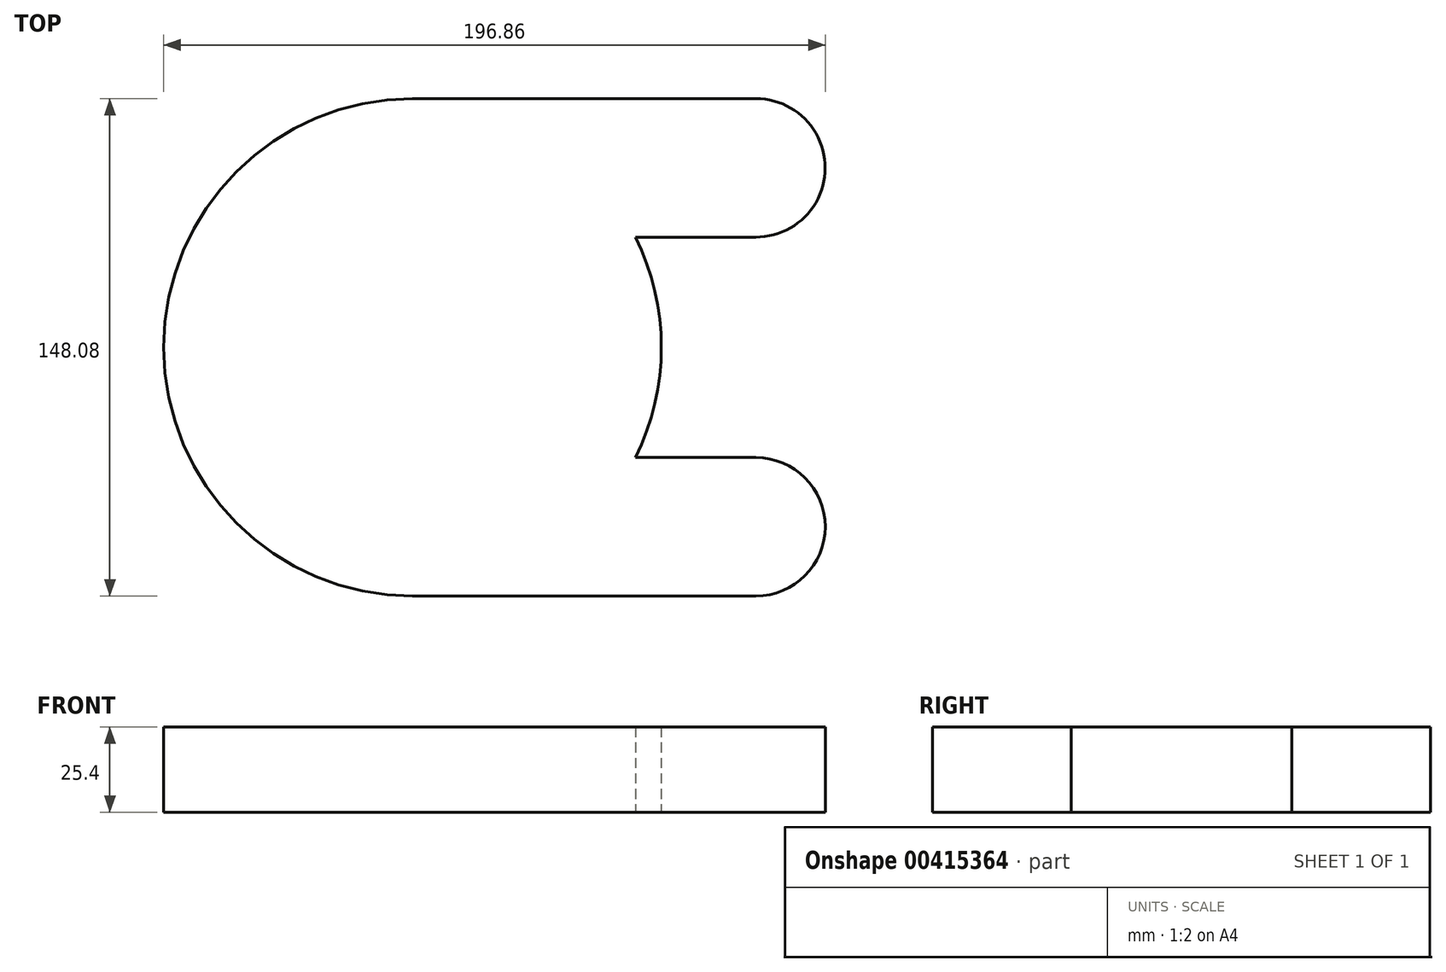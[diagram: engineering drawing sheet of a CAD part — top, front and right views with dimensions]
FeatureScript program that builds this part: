
annotation { "Feature Type Name" : "Feature", "Feature Type Description" : "" }
export const myFeature = defineFeature(function(context is Context, id is Id, definition is map)
    precondition{}
    {
        {
            var Q0;
            Q0=qCreatedBy(makeId("Top.planeOp"),FACE);
            var sketch = newSketch(context, id + "F0", { "sketchPlane" : qUnion([Q0])});
            skCircle(sketch, "E0", {"center": v(0, 0) * mm, "radius": 74.04 * mm});
            skCircle(sketch, "E1", {"center": v(0, 0) * mm, "radius": 53.43 * mm});
            skCircle(sketch, "E2", {"center": v(0, 53.43) * mm, "radius": 20.6 * mm});
            skCircle(sketch, "E3", {"center": v(0, -53.43) * mm, "radius": 20.6 * mm});
            skCircle(sketch, "E4", {"center": v(102.2, -53.43) * mm, "radius": 20.6 * mm});
            skCircle(sketch, "E5", {"center": v(102.2, 53.43) * mm, "radius": 20.6 * mm});
            skLineSegment(sketch, "E6", {"start": v(0, -53.43) * mm, "end": v(102.2, -53.43) * mm});
            skLineSegment(sketch, "E7", {"start": v(0, 53.43) * mm, "end": v(102.2, 53.43) * mm});
            skLineSegment(sketch, "E8", {"start": v(0, 0) * mm, "end": v(102.2, 0) * mm});
            skLineSegment(sketch, "E9", {"start": v(0, 74.04) * mm, "end": v(102.2, 74.04) * mm});
            skLineSegment(sketch, "E10", {"start": v(0, -74.04) * mm, "end": v(102.2, -74.04) * mm});
            skLineSegment(sketch, "E11", {"start": v(102.2, -74.04) * mm, "end": v(102.2, -74.04) * mm});
            skLineSegment(sketch, "E12", {"start": v(102.2, 74.04) * mm, "end": v(102.2, 53.43) * mm});
            skLineSegment(sketch, "E13", {"start": v(102.2, 0) * mm, "end": v(102.2, 53.43) * mm});
            skLineSegment(sketch, "E14", {"start": v(102.2, 0) * mm, "end": v(102.2, -53.43) * mm});
            skLineSegment(sketch, "E15", {"start": v(102.2, -53.43) * mm, "end": v(102.2, -74.04) * mm});
            skLineSegment(sketch, "E16", {"start": v(102.2, -32.82) * mm, "end": v(0, -32.82) * mm});
            skLineSegment(sketch, "E17", {"start": v(0.09, 32.82) * mm, "end": v(102.2, 32.82) * mm});
            skSolve(sketch);
        }
        {
            var Q0;
            {var subQ0=sQuery(id+"F0.wireOp",EDGE,"E1");var subQ1=makeQuery(id+"F0.imprint","INTERSECT",VERTEX,{"derivedFrom":[subQ0,sQuery(id+"F0.wireOp",EDGE,"E8")]});Q0=makeQuery(id+"F0.imprint","IMPRINT",FACE,{"disambiguationData":[TD([[makeQuery(id+"F0.imprint","IMPRINT",EDGE,{"disambiguationData":[TD([[subQ1,-1.0]])],"derivedFrom":subQ0}),1.0]])]});}
            var Q1;
            {var subQ0=sQuery(id+"F0.wireOp",EDGE,"E1");var subQ1=makeQuery(id+"F0.imprint","INTERSECT",VERTEX,{"derivedFrom":[subQ0,sQuery(id+"F0.wireOp",EDGE,"E6")]});Q1=makeQuery(id+"F0.imprint","IMPRINT",FACE,{"disambiguationData":[TD([[makeQuery(id+"F0.imprint","IMPRINT",EDGE,{"disambiguationData":[TD([[subQ1,1.0]])],"derivedFrom":subQ0}),1.0]])]});}
            var Q2;
            {var subQ0=sQuery(id+"F0.wireOp",EDGE,"E3");var subQ1=sQuery(id+"F0.wireOp",EDGE,"E1");var subQ2=makeQuery(id+"F0.imprint","INTERSECT",VERTEX,{"disambiguationData":[OD(1.0)],"derivedFrom":[subQ1,subQ0]});Q2=makeQuery(id+"F0.imprint","IMPRINT",FACE,{"disambiguationData":[TD([[makeQuery(id+"F0.imprint","IMPRINT",EDGE,{"disambiguationData":[TD([[subQ2,-1.0]])],"derivedFrom":subQ1}),1.0]])]});}
            var Q3;
            {var subQ0=sQuery(id+"F0.wireOp",EDGE,"E6");var subQ1=sQuery(id+"F0.wireOp",EDGE,"E1");var subQ2=makeQuery(id+"F0.imprint","INTERSECT",VERTEX,{"derivedFrom":[subQ1,subQ0]});Q3=makeQuery(id+"F0.imprint","IMPRINT",FACE,{"disambiguationData":[TD([[makeQuery(id+"F0.imprint","IMPRINT",EDGE,{"disambiguationData":[TD([[subQ2,-1.0]])],"derivedFrom":subQ1}),-1.0]])]});}
            var Q4;
            {var subQ3=sQuery(id+"F0.wireOp",EDGE,"E6");var subQ7=sQuery(id+"F0.wireOp",EDGE,"E0");var subQ8=makeQuery(id+"F0.imprint","INTERSECT",VERTEX,{"derivedFrom":[subQ7,subQ3]});Q4=makeQuery(id+"F0.imprint","IMPRINT",FACE,{"disambiguationData":[TD([[makeQuery(id+"F0.imprint","IMPRINT",EDGE,{"disambiguationData":[TD([[subQ8,-1.0]])],"derivedFrom":subQ7}),1.0]])]});}
            var Q5;
            {var subQ1=sQuery(id+"F0.wireOp",EDGE,"E4");var subQ3=sQuery(id+"F0.wireOp",EDGE,"E6");var subQ4=makeQuery(id+"F0.imprint","INTERSECT",VERTEX,{"derivedFrom":[subQ1,subQ3]});Q5=makeQuery(id+"F0.imprint","IMPRINT",FACE,{"disambiguationData":[TD([[makeQuery(id+"F0.imprint","IMPRINT",EDGE,{"disambiguationData":[TD([[subQ4,1.0]])],"derivedFrom":subQ1}),1.0]])]});}
            var Q6;
            {var subQ0=sQuery(id+"F0.wireOp",EDGE,"E7");var subQ1=sQuery(id+"F0.wireOp",EDGE,"E1");var subQ2=makeQuery(id+"F0.imprint","INTERSECT",VERTEX,{"derivedFrom":[subQ1,subQ0]});Q6=makeQuery(id+"F0.imprint","IMPRINT",FACE,{"disambiguationData":[TD([[makeQuery(id+"F0.imprint","IMPRINT",EDGE,{"disambiguationData":[TD([[subQ2,-1.0]])],"derivedFrom":subQ1}),-1.0]])]});}
            var Q7;
            {var subQ1=sQuery(id+"F0.wireOp",EDGE,"E0");var subQ3=sQuery(id+"F0.wireOp",EDGE,"E7");var subQ4=makeQuery(id+"F0.imprint","INTERSECT",VERTEX,{"derivedFrom":[subQ1,subQ3]});Q7=makeQuery(id+"F0.imprint","IMPRINT",FACE,{"disambiguationData":[TD([[makeQuery(id+"F0.imprint","IMPRINT",EDGE,{"disambiguationData":[TD([[subQ4,1.0]])],"derivedFrom":subQ3}),1.0]])]});}
            var Q8;
            {var subQ0=sQuery(id+"F0.wireOp",EDGE,"E15");Q8=makeQuery(id+"F0.imprint","IMPRINT",FACE,{"disambiguationData":[TD([[makeQuery(id+"F0.imprint","IMPRINT",EDGE,{"derivedFrom":subQ0}),-1.0]])]});}
            var Q9;
            {var subQ0=sQuery(id+"F0.wireOp",EDGE,"E9");Q9=makeQuery(id+"F0.imprint","IMPRINT",FACE,{"disambiguationData":[TD([[makeQuery(id+"F0.imprint","IMPRINT",EDGE,{"derivedFrom":subQ0}),-1.0]])]});}
            var Q10;
            {var subQ0=sQuery(id+"F0.wireOp",EDGE,"E6");var subQ1=sQuery(id+"F0.wireOp",EDGE,"E1");var subQ2=makeQuery(id+"F0.imprint","INTERSECT",VERTEX,{"derivedFrom":[subQ1,subQ0]});Q10=makeQuery(id+"F0.imprint","IMPRINT",FACE,{"disambiguationData":[TD([[makeQuery(id+"F0.imprint","IMPRINT",EDGE,{"disambiguationData":[TD([[subQ2,1.0]])],"derivedFrom":subQ1}),-1.0]])]});}
            var Q11;
            {var subQ0=sQuery(id+"F0.wireOp",EDGE,"E12");Q11=makeQuery(id+"F0.imprint","IMPRINT",FACE,{"disambiguationData":[TD([[makeQuery(id+"F0.imprint","IMPRINT",EDGE,{"derivedFrom":subQ0}),1.0]])]});}
            var Q12;
            {var subQ0=sQuery(id+"F0.wireOp",EDGE,"E12");Q12=makeQuery(id+"F0.imprint","IMPRINT",FACE,{"disambiguationData":[TD([[makeQuery(id+"F0.imprint","IMPRINT",EDGE,{"derivedFrom":subQ0}),-1.0]])]});}
            var Q13;
            {var subQ1=sQuery(id+"F0.wireOp",EDGE,"E0");var subQ3=sQuery(id+"F0.wireOp",EDGE,"E6");var subQ4=makeQuery(id+"F0.imprint","INTERSECT",VERTEX,{"derivedFrom":[subQ1,subQ3]});Q13=makeQuery(id+"F0.imprint","IMPRINT",FACE,{"disambiguationData":[TD([[makeQuery(id+"F0.imprint","IMPRINT",EDGE,{"disambiguationData":[TD([[subQ4,1.0]])],"derivedFrom":subQ3}),-1.0]])]});}
            var Q14;
            {var subQ0=sQuery(id+"F0.wireOp",EDGE,"E10");Q14=makeQuery(id+"F0.imprint","IMPRINT",FACE,{"disambiguationData":[TD([[makeQuery(id+"F0.imprint","IMPRINT",EDGE,{"derivedFrom":subQ0}),1.0]])]});}
            var Q15;
            {var subQ0=sQuery(id+"F0.wireOp",EDGE,"E2");var subQ5=sQuery(id+"F0.wireOp",EDGE,"E1");var subQ6=makeQuery(id+"F0.imprint","INTERSECT",VERTEX,{"disambiguationData":[OD(1.0)],"derivedFrom":[subQ5,subQ0]});Q15=makeQuery(id+"F0.imprint","IMPRINT",FACE,{"disambiguationData":[TD([[makeQuery(id+"F0.imprint","IMPRINT",EDGE,{"disambiguationData":[TD([[subQ6,-1.0]])],"derivedFrom":subQ5}),-1.0]])]});}
            var Q16;
            {var subQ0=sQuery(id+"F0.wireOp",EDGE,"E6");var subQ1=sQuery(id+"F0.wireOp",EDGE,"E0");var subQ2=makeQuery(id+"F0.imprint","INTERSECT",VERTEX,{"derivedFrom":[subQ1,subQ0]});Q16=makeQuery(id+"F0.imprint","IMPRINT",FACE,{"disambiguationData":[TD([[makeQuery(id+"F0.imprint","IMPRINT",EDGE,{"disambiguationData":[TD([[subQ2,-1.0]])],"derivedFrom":subQ1}),-1.0]])]});}
            var Q17;
            {var subQ0=sQuery(id+"F0.wireOp",EDGE,"E13");var subQ1=sQuery(id+"F0.wireOp",EDGE,"E5");var subQ2=makeQuery(id+"F0.imprint","INTERSECT",VERTEX,{"derivedFrom":[subQ1,subQ0]});Q17=makeQuery(id+"F0.imprint","IMPRINT",FACE,{"disambiguationData":[TD([[makeQuery(id+"F0.imprint","IMPRINT",EDGE,{"disambiguationData":[TD([[subQ2,1.0]])],"derivedFrom":subQ1}),1.0]])]});}
            var Q18;
            {var subQ0=sQuery(id+"F0.wireOp",EDGE,"E15");Q18=makeQuery(id+"F0.imprint","IMPRINT",FACE,{"disambiguationData":[TD([[makeQuery(id+"F0.imprint","IMPRINT",EDGE,{"derivedFrom":subQ0}),1.0]])]});}
            var Q19;
            {var subQ0=sQuery(id+"F0.wireOp",EDGE,"E7");var subQ1=sQuery(id+"F0.wireOp",EDGE,"E5");var subQ2=makeQuery(id+"F0.imprint","INTERSECT",VERTEX,{"derivedFrom":[subQ1,subQ0]});Q19=makeQuery(id+"F0.imprint","IMPRINT",FACE,{"disambiguationData":[TD([[makeQuery(id+"F0.imprint","IMPRINT",EDGE,{"disambiguationData":[TD([[subQ2,-1.0]])],"derivedFrom":subQ1}),1.0]])]});}
            var Q20;
            {var subQ0=sQuery(id+"F0.wireOp",EDGE,"E7");var subQ1=sQuery(id+"F0.wireOp",EDGE,"E0");var subQ2=makeQuery(id+"F0.imprint","INTERSECT",VERTEX,{"derivedFrom":[subQ1,subQ0]});Q20=makeQuery(id+"F0.imprint","IMPRINT",FACE,{"disambiguationData":[TD([[makeQuery(id+"F0.imprint","IMPRINT",EDGE,{"disambiguationData":[TD([[subQ2,1.0]])],"derivedFrom":subQ1}),-1.0]])]});}
            var Q21;
            {var subQ3=sQuery(id+"F0.wireOp",EDGE,"E7");var subQ7=sQuery(id+"F0.wireOp",EDGE,"E0");var subQ8=makeQuery(id+"F0.imprint","INTERSECT",VERTEX,{"derivedFrom":[subQ7,subQ3]});Q21=makeQuery(id+"F0.imprint","IMPRINT",FACE,{"disambiguationData":[TD([[makeQuery(id+"F0.imprint","IMPRINT",EDGE,{"disambiguationData":[TD([[subQ8,1.0]])],"derivedFrom":subQ7}),1.0]])]});}
            var Q22;
            {var subQ0=sQuery(id+"F0.wireOp",EDGE,"E7");var subQ1=sQuery(id+"F0.wireOp",EDGE,"E1");var subQ2=makeQuery(id+"F0.imprint","INTERSECT",VERTEX,{"derivedFrom":[subQ1,subQ0]});Q22=makeQuery(id+"F0.imprint","IMPRINT",FACE,{"disambiguationData":[TD([[makeQuery(id+"F0.imprint","IMPRINT",EDGE,{"disambiguationData":[TD([[subQ2,1.0]])],"derivedFrom":subQ1}),-1.0]])]});}
            var Q23;
            {var subQ0=sQuery(id+"F0.wireOp",EDGE,"E1");var subQ1=makeQuery(id+"F0.imprint","INTERSECT",VERTEX,{"derivedFrom":[subQ0,sQuery(id+"F0.wireOp",EDGE,"E7")]});Q23=makeQuery(id+"F0.imprint","IMPRINT",FACE,{"disambiguationData":[TD([[makeQuery(id+"F0.imprint","IMPRINT",EDGE,{"disambiguationData":[TD([[subQ1,1.0]])],"derivedFrom":subQ0}),1.0]])]});}
            var Q24;
            {var subQ0=sQuery(id+"F0.wireOp",EDGE,"E17");var subQ1=sQuery(id+"F0.wireOp",EDGE,"E0");var subQ2=makeQuery(id+"F0.imprint","INTERSECT",VERTEX,{"derivedFrom":[subQ1,subQ0]});Q24=makeQuery(id+"F0.imprint","IMPRINT",FACE,{"disambiguationData":[TD([[makeQuery(id+"F0.imprint","IMPRINT",EDGE,{"disambiguationData":[TD([[subQ2,1.0]])],"derivedFrom":subQ1}),1.0]])]});}
            var Q25;
            {var subQ0=sQuery(id+"F0.wireOp",EDGE,"E16");var subQ1=sQuery(id+"F0.wireOp",EDGE,"E0");var subQ2=makeQuery(id+"F0.imprint","INTERSECT",VERTEX,{"derivedFrom":[subQ1,subQ0]});Q25=makeQuery(id+"F0.imprint","IMPRINT",FACE,{"disambiguationData":[TD([[makeQuery(id+"F0.imprint","IMPRINT",EDGE,{"disambiguationData":[TD([[subQ2,-1.0]])],"derivedFrom":subQ1}),1.0]])]});}
            var Q26;
            {var subQ0=sQuery(id+"F0.wireOp",EDGE,"E17");var subQ1=sQuery(id+"F0.wireOp",EDGE,"E1");var subQ2=makeQuery(id+"F0.imprint","INTERSECT",VERTEX,{"derivedFrom":[subQ1,subQ0]});Q26=makeQuery(id+"F0.imprint","IMPRINT",FACE,{"disambiguationData":[TD([[makeQuery(id+"F0.imprint","IMPRINT",EDGE,{"disambiguationData":[TD([[subQ2,-1.0]])],"derivedFrom":subQ1}),1.0]])]});}
            extrude(context, id + "F1", {"entities" : qUnion([Q0, Q1, Q2, Q3, Q4, Q5, Q6, Q7, Q8, Q9, Q10, Q11, Q12, Q13, Q14, Q15, Q16, Q17, Q18, Q19, Q20, Q21, Q22, Q23, Q24, Q25, Q26]), "depth" : 25.4 * mm});
        }
    });
